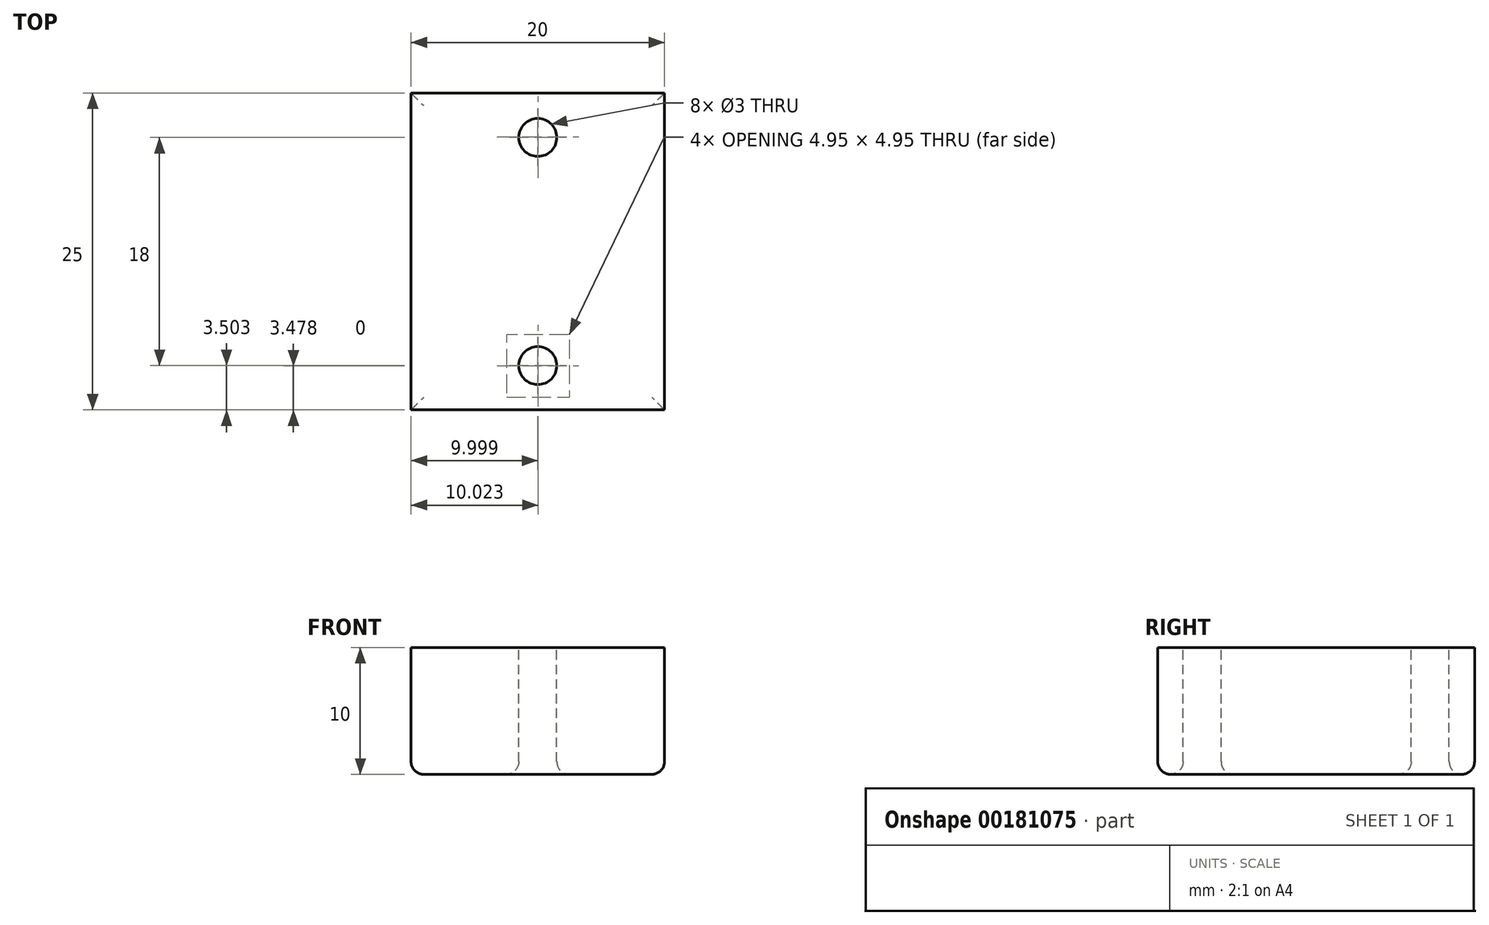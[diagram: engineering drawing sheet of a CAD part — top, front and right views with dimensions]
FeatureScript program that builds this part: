
annotation { "Feature Type Name" : "Feature", "Feature Type Description" : "" }
export const myFeature = defineFeature(function(context is Context, id is Id, definition is map)
    precondition{}
    {
        {
            var Q0;
            Q0=qCreatedBy(makeId("Top.planeOp"),FACE);
            var sketch = newSketch(context, id + "F0", { "sketchPlane" : qUnion([Q0])});
            skLineSegment(sketch, "E0.bottom", {"start": v(-21.37, 11.7) * mm, "end": v(-1.37, 11.7) * mm});
            skLineSegment(sketch, "E0.top", {"start": v(-21.37, -13.3) * mm, "end": v(-1.37, -13.3) * mm});
            skLineSegment(sketch, "E0.left", {"start": v(-21.37, 11.7) * mm, "end": v(-21.37, -13.3) * mm});
            skLineSegment(sketch, "E0.right", {"start": v(-1.37, 11.7) * mm, "end": v(-1.37, -13.3) * mm});
            skSolve(sketch);
        }
        {
            var Q0;
            Q0 = qSketchRegion(id + "F0", true);
            extrude(context, id + "F1", {"entities" : qUnion([Q0]), "depth" : 10 * mm});
        }
        {
            var Q0;
            Q0=makeQuery(id+"F1.opExtrude","CAP_FACE",FACE,{"disambiguationData":[OSD([sQuery(id+"F0.wireOp",EDGE,"E0.bottom"),sQuery(id+"F0.wireOp",EDGE,"E0.top"),sQuery(id+"F0.wireOp",EDGE,"E0.left"),sQuery(id+"F0.wireOp",EDGE,"E0.right")])],"isStart":false});
            var sketch = newSketch(context, id + "F2", { "sketchPlane" : qUnion([Q0])});
            skPoint(sketch, "E1", {"position": v(-11.37, 8.2) * mm});
            skPoint(sketch, "E1.positionSnap0", {"position": v(-11.37, 11.7) * mm});
            skPoint(sketch, "E2", {"position": v(-11.37, -9.8) * mm});
            skPoint(sketch, "E2.positionSnap0", {"position": v(-11.37, -13.3) * mm});
            skSolve(sketch);
        }
        {
            var Q0;
            Q0=sQuery(id+"F2.wireOp",VERTEX,"E1");
            var Q1;
            Q1=sQuery(id+"F2.wireOp",VERTEX,"E2");
            var Q2;
            Q2=makeQuery(id+"F1.opExtrude","SWEPT_BODY",BODY,{"disambiguationData":[OSD([sQuery(id+"F0.wireOp",EDGE,"E0.bottom"),sQuery(id+"F0.wireOp",EDGE,"E0.top"),sQuery(id+"F0.wireOp",EDGE,"E0.left"),sQuery(id+"F0.wireOp",EDGE,"E0.right")])]});
            hole(context, id + "F3", {"style" : HoleStyle.SIMPLE, "endStyle" : HoleEndStyle.BLIND, "holeDiameter" : 3 * mm, "holeDepth" : 10 * mm, "locations" : qUnion([Q0, Q1]), "scope" : qUnion([Q2])});
        }
        {
            var Q0;
            Q0=makeQuery(id+"F1.opExtrude","CAP_FACE",FACE,{"disambiguationData":[OSD([sQuery(id+"F0.wireOp",EDGE,"E0.bottom"),sQuery(id+"F0.wireOp",EDGE,"E0.top"),sQuery(id+"F0.wireOp",EDGE,"E0.left"),sQuery(id+"F0.wireOp",EDGE,"E0.right")])],"isStart":true});
            fillet(context, id + "F4", {"entities" : qUnion([Q0]), "radius" : 1 * mm, "tangentPropagation" : true, "allowEdgeOverflow" : false});
        }
    });
